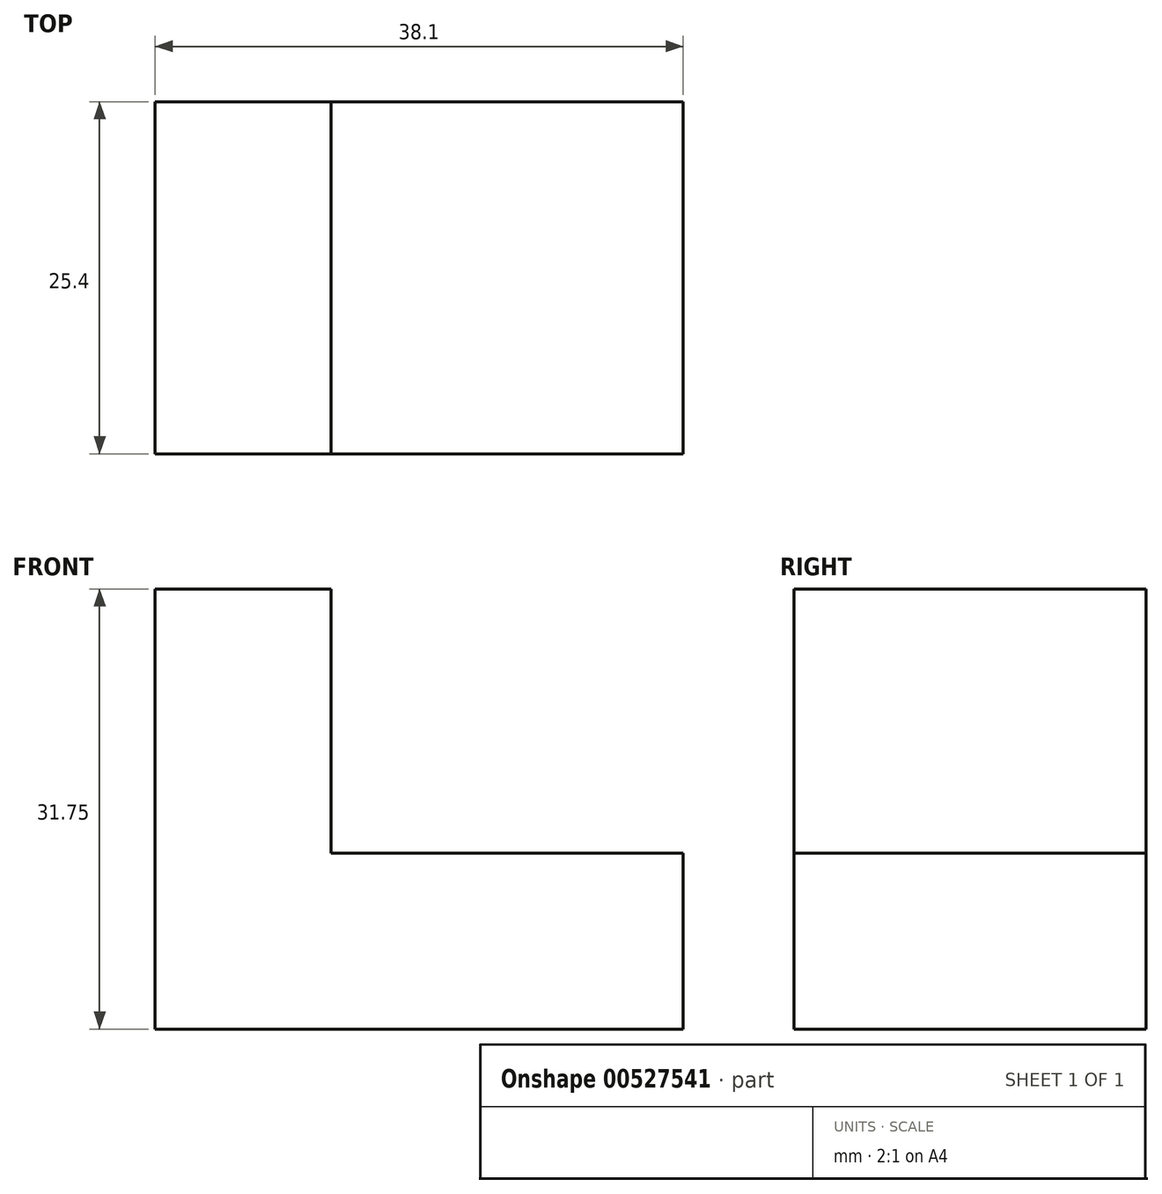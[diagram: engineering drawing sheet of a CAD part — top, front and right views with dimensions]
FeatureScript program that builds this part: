
annotation { "Feature Type Name" : "Feature", "Feature Type Description" : "" }
export const myFeature = defineFeature(function(context is Context, id is Id, definition is map)
    precondition{}
    {
        {
            var Q0;
            Q0=qCreatedBy(makeId("Front.planeOp"),FACE);
            var sketch = newSketch(context, id + "F0", { "sketchPlane" : qUnion([Q0])});
            skLineSegment(sketch, "E0", {"start": v(0, 0) * mm, "end": v(38.1, 0) * mm});
            skLineSegment(sketch, "E1", {"start": v(38.1, 0) * mm, "end": v(38.1, 12.7) * mm});
            skLineSegment(sketch, "E2", {"start": v(38.1, 12.7) * mm, "end": v(12.7, 12.7) * mm});
            skLineSegment(sketch, "E3", {"start": v(12.7, 12.7) * mm, "end": v(12.7, 31.75) * mm});
            skLineSegment(sketch, "E4", {"start": v(12.7, 31.75) * mm, "end": v(0, 31.75) * mm});
            skLineSegment(sketch, "E5", {"start": v(0, 0) * mm, "end": v(0, 31.75) * mm});
            skSolve(sketch);
        }
        {
            var Q0;
            Q0=makeQuery(id+"F0.imprint","IMPRINT",FACE,{"disambiguationData":[TD([[makeQuery(id+"F0.imprint","IMPRINT",EDGE,{"derivedFrom":sQuery(id+"F0.wireOp",EDGE,"E0")}),1.0]])]});
            extrude(context, id + "F1", {"entities" : qUnion([Q0]), "depth" : 25.4 * mm, "offsetDistance" : 25.4 * mm});
        }
    });
